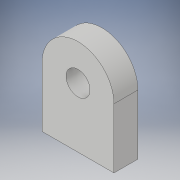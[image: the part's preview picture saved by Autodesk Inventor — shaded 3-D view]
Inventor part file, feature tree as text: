
AUTODESK INVENTOR PART (.ipt)
format: ipt  version: 2019.4 (Build 234330000, 330)  size: 99,840 bytes
history: native  units: mm
features: other x1, extrude x1, sketch x1
ambient origin geometry x8: Origin, YZ Plane, XZ Plane, XY Plane, X Axis, Y Axis, Z Axis, Center Point
bodies: Body1 (feature_tree)
feature tree (3):
  other  "Sólido1"
  extrude  "Extrusión1"  Depth=300.0mm
  sketch  "Boceto1"  dims[d0=100.0mm d1=300.0mm d4=300.0mm d5=100.0mm d6=0.0mm]
